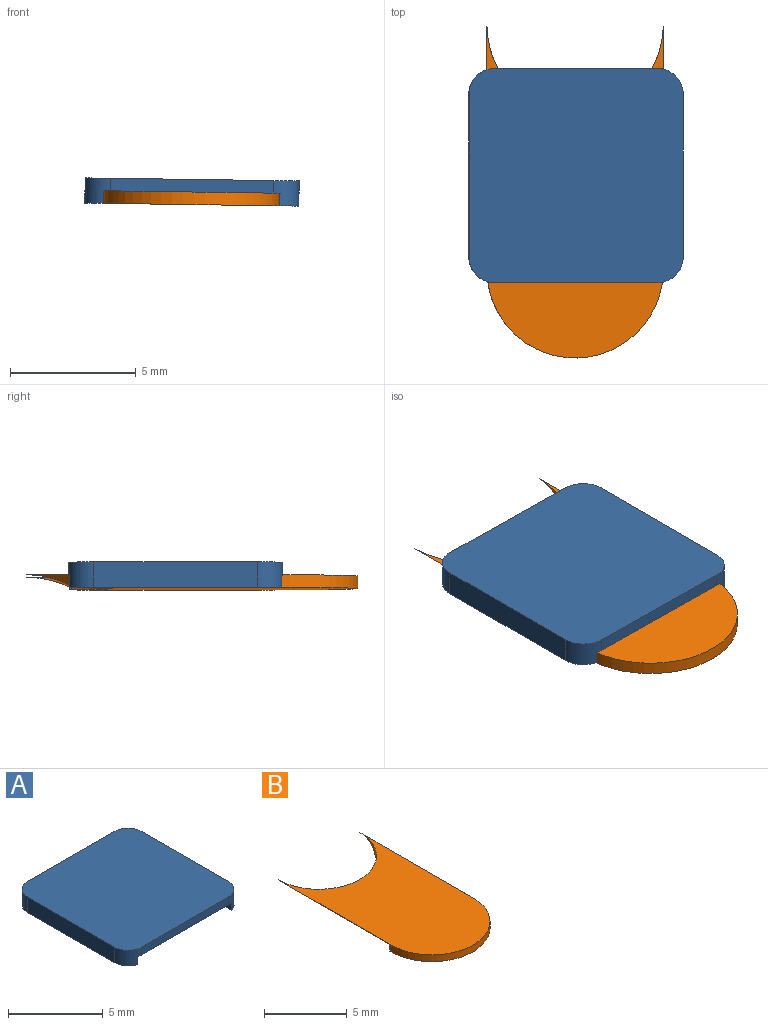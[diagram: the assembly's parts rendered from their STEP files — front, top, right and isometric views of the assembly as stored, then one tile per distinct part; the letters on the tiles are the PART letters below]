
ASSEMBLY  parts=2 mates=1
PART A: 30 faces, bbox 8.5x8.5x1 mm
  f0: plane 8.44x1.35mm, normal (0,0,-1), area 6.3mm2, adj f2,f4,f6,f10,f18,f19,f27,f28
  f1: cylinder r=1mm len=1mm, axis (0,0,-1), area 1.4mm2, adj f3,f5,f7,f9,f12,f13,f24,f26
  f2: cylinder r=1mm len=1mm, axis (0,0,1), area 1.4mm2, adj f0,f6,f7,f10,f12,f14,f28,f29
  f3: plane 8.45x0.58mm, normal (-0.66,0,0.75), area 0.5mm2, adj f1,f5,f8,f13,f22,f23,f25,f26
  f4: cylinder r=1mm len=1mm, axis (0,0,-1), area 1.4mm2, adj f0,f6,f10,f11,f12,f14,f19,f20
  f5: plane 8.44x1.34mm, normal (0,0,-1), area 6.3mm2, adj f1,f3,f8,f9,f21,f22,f24,f25
  f6: plane 8.45x0.6mm, normal (0.64,0,0.76), area 0.6mm2, adj f0,f2,f4,f14,f18,f20,f27,f29
  f7: plane 6.5x0.5mm, normal (0,1,0), area 3.2mm2, adj f1,f2,f12,f15,f16,f17
  f8: cylinder r=1mm len=1mm, axis (0,0,1), area 1.4mm2, adj f3,f5,f9,f11,f12,f13,f21,f23
  f9: plane 6.5x1mm, normal (1,0,0), area 6.5mm2, adj f1,f5,f8,f12
  f10: plane 6.5x1mm, normal (-1,0,0), area 6.5mm2, adj f0,f2,f4,f12
  f11: plane 6.5x0.5mm, normal (0,-1,0), area 3.3mm2, adj f4,f8,f12,f15,f16,f17
  f12: plane 8.5x8.5mm, normal (0,0,1), area 71.4mm2, adj f1,f2,f4,f7,f8,f9,f10,f11
  f13: plane 8.5x0.24mm, normal (0,0,-1), area 2mm2, adj f1,f3,f8,f17
  f14: plane 8.5x0.25mm, normal (0,0,-1), area 2.1mm2, adj f2,f4,f6,f15
  f15: plane 8.5x0.01mm, normal (-1,0,0), area 0.1mm2, adj f7,f11,f14,f16
  f16: plane 8.5x6.5mm, normal (0,0,-1), area 55.3mm2, adj f7,f11,f15,f17
  f17: plane 8.5x0mm, normal (1,0,0), area 0mm2, adj f7,f11,f13,f16
  f18: plane 0.6x0.49mm, normal (0,-1,0), area 0.1mm2, adj f0,f6,f19,f20
  f19: plane 6.17x0.49mm, normal (1,0,0), area 3mm2, adj f0,f4,f18,f20
  f20: plane 6.17x0.02mm, normal (0,0,-1), area 0.1mm2, adj f4,f6,f18,f19
  f21: plane 6.17x0.49mm, normal (-1,0,0), area 3mm2, adj f5,f8,f22,f23
  f22: plane 0.59x0.49mm, normal (0,-1,0), area 0.2mm2, adj f3,f5,f21,f23
  f23: plane 6.17x0.03mm, normal (0,0,-1), area 0.2mm2, adj f3,f8,f21,f22
  f24: plane 1.79x0.49mm, normal (-1,0,0), area 0.9mm2, adj f1,f5,f25,f26
  f25: plane 0.59x0.49mm, normal (0,1,0), area 0.2mm2, adj f3,f5,f24,f26
  f26: plane 1.8x0.03mm, normal (0,0,-1), area 0mm2, adj f1,f3,f24,f25
  f27: plane 0.59x0.49mm, normal (0,1,0), area 0.1mm2, adj f0,f6,f28,f29
  f28: plane 1.79x0.49mm, normal (1,0,0), area 0.9mm2, adj f0,f2,f27,f29
  f29: plane 1.79x0.01mm, normal (0,0,-1), area 0mm2, adj f2,f6,f27,f28
PART B: 10 faces, bbox 7x13.2x0.5 mm
  f0: plane 9.53x0.5mm, normal (1,0,0), area 0.1mm2, adj f2,f4,f5,f6,f7
  f1: cylinder r=3.5mm len=7mm, axis (0,0,-1), area 4.1mm2, adj f2,f5,f6,f8
  f2: plane 13.19x7mm, normal (0,0,1), area 68mm2, adj f0,f1,f3,f4,f6,f8
  f3: plane 8.43x0.5mm, normal (-1,0,0), area 0mm2, adj f2,f4,f5,f8,f9
  f4: cylinder r=3.5mm len=7mm, axis (0,0,-1), area 5.5mm2, adj f0,f2,f3,f5
  f5: plane 11.29x7mm, normal (0,0,-1), area 58.4mm2, adj f0,f1,f3,f4,f6,f7,f8,f9
  f6: plane 9.58x0.58mm, normal (0.66,0,-0.76), area 6.3mm2, adj f0,f1,f2,f5,f7
  f7: plane 0.57x0.5mm, normal (0,1,0), area 0.1mm2, adj f0,f5,f6
  f8: plane 9.58x0.58mm, normal (-0.66,0,-0.76), area 6.3mm2, adj f1,f2,f3,f5,f9
  f9: plane 0.58x0.5mm, normal (0,1,0), area 0.1mm2, adj f3,f5,f8
PLACE A rot(axis=(-0.01,0,-1),180deg) t=(-3.55,-21.79,8.28)mm
PLACE B rot(axis=(0,1,0),0.8deg) t=(-3.58,-11.7,8.29)mm
MATE planar A.f16 <-> B.f2  axis (-0.01,0,-1) through (-3.54,-17.67,8.78)mm
